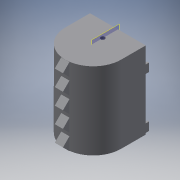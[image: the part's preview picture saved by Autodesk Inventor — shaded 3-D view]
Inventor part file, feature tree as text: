
AUTODESK INVENTOR PART (.ipt)
format: ipt  version: 2016 (Build 200138000, 138)  size: 216,064 bytes
history: native  units: in
note: dims shown in document units (in); Inventor stores cm internally (conversion verified against a paired STEP export)
features: reference x10, sketch x9, extrude x8, plane x1
ambient origin geometry x8: Origin, YZ Plane, XZ Plane, XY Plane, X Axis, Y Axis, Z Axis, Center Point
bodies: Solid1 (feature_tree)
feature tree (28):
  extrude  "Extrusion1"  Depth=1.5in TaperAngle=0.0deg
  extrude  "Extrusion2"  Depth=0.1969in TaperAngle=0.0deg
  extrude  "Extrusion3"  [1 undecoded]
  extrude  "Extrusion4"  Depth=0.3937in
  plane  "Work Plane1"
  sketch  "Sketch5"  dims[d12=1.9685in d14=0.9774in d15=0.3937in d17=1.0in d19=0.5in d20=0.0in]
  extrude  "Extrusion5"  Depth=0.5in TaperAngle=0.0deg
  extrude  "Extrusion6"  Depth=2.0in TaperAngle=0.0deg
  extrude  "Extrusion7"  [1 undecoded]
  extrude  "Extrusion8"  [1 undecoded]
  sketch  "Sketch1"  dims[d0=0.1969in d1=1.5in d2=0.0in]
  reference  "Reference1"
  sketch  "Sketch2"  dims[d3=4.6969in d4=0.0in d5=0.1969in d6=0.0in]
  sketch  "Sketch3"  dims[d7=0.1969in d8=0.0in d9=-1.697in]
  sketch  "Sketch4"  dims[d10=0.7874in d11=0.3937in]
  reference  "Reference2"
  sketch  "Sketch6"  dims[d21=0.197in d22=0.0in d23=2.0in d24=0.0in]
  sketch  "Sketch8"  dims[d25=2.0in d26=0.0in]
  reference  "Reference3"
  reference  "Reference5"
  reference  "Reference6"
  reference  "Reference7"
  reference  "Reference8"
  reference  "Reference9"
  sketch  "Sketch9"
  reference  "Reference10"
  sketch  "Sketch10"
  reference  "Reference11"
note: 3 required parameter values undecoded (feature->parameter linkage not recoverable at this tier; creation-order binding heuristic only, values carry confidence <= 0.55)
